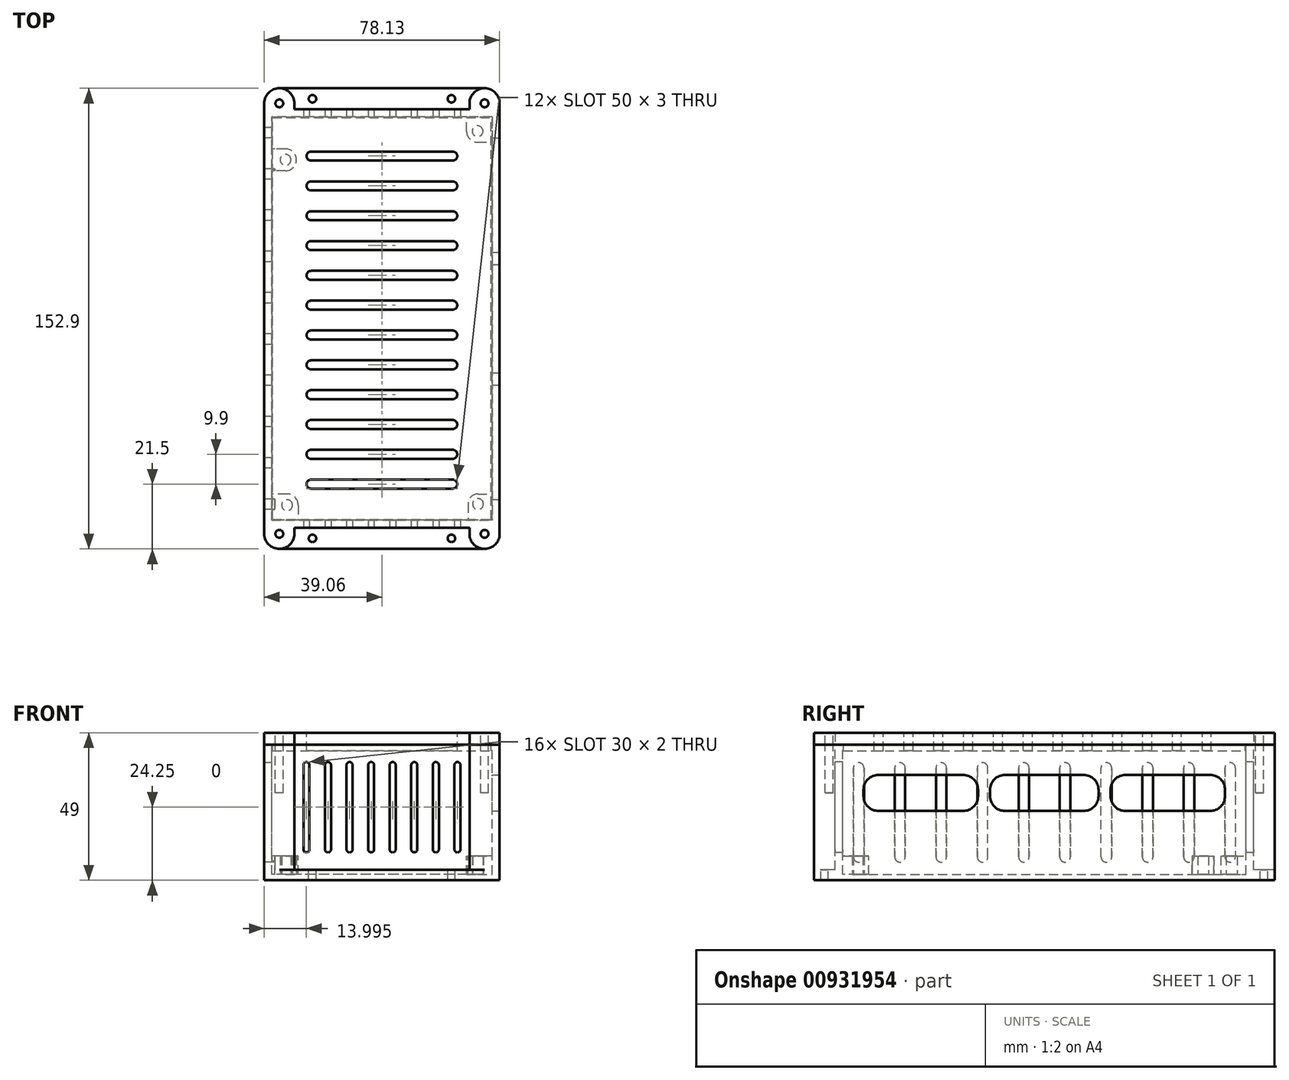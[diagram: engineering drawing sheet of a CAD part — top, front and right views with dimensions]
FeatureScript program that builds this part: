
annotation { "Feature Type Name" : "Feature", "Feature Type Description" : "" }
export const myFeature = defineFeature(function(context is Context, id is Id, definition is map)
    precondition{}
    {
        {
            var Q0;
            Q0=qCreatedBy(makeId("Top.planeOp"),FACE);
            var sketch = newSketch(context, id + "F0", { "sketchPlane" : qUnion([Q0])});
            skPoint(sketch, "E0.middle", {"position": v(0, 0) * mm});
            skLineSegment(sketch, "E1.0", {"start": v(33.87, 64.25) * mm, "end": v(-37.26, 64.25) * mm});
            skLineSegment(sketch, "E1.1", {"start": v(33.87, 64.25) * mm, "end": v(33.87, -67.65) * mm});
            skLineSegment(sketch, "E1.2", {"start": v(33.87, -67.65) * mm, "end": v(-37.26, -67.65) * mm});
            skLineSegment(sketch, "E1.3", {"start": v(-37.26, 64.25) * mm, "end": v(-37.26, -67.65) * mm});
            skLineSegment(sketch, "E2.0", {"start": v(37.37, -71.15) * mm, "end": v(-40.76, -71.15) * mm});
            skLineSegment(sketch, "E2.1", {"start": v(37.37, 67.75) * mm, "end": v(37.37, -71.15) * mm});
            skLineSegment(sketch, "E2.2", {"start": v(37.37, 67.75) * mm, "end": v(-40.76, 67.75) * mm});
            skLineSegment(sketch, "E2.3", {"start": v(-40.76, 67.75) * mm, "end": v(-40.76, -71.15) * mm});
            skSolve(sketch);
        }
        {
            var Q0;
            Q0 = qSketchRegion(id + "F0", true);
            extrude(context, id + "F1", {"entities" : qUnion([Q0]), "depth" : 25 * mm, "offsetDistance" : 25 * mm});
        }
        {
            var Q0;
            Q0=makeQuery(id+"F1.opExtrude","CAP_FACE",FACE,{"disambiguationData":[OSD([sQuery(id+"F0.wireOp",EDGE,"E1.0"),sQuery(id+"F0.wireOp",EDGE,"E1.1"),sQuery(id+"F0.wireOp",EDGE,"E1.2"),sQuery(id+"F0.wireOp",EDGE,"E1.3"),sQuery(id+"F0.wireOp",EDGE,"E2.0"),sQuery(id+"F0.wireOp",EDGE,"E2.1"),sQuery(id+"F0.wireOp",EDGE,"E2.2"),sQuery(id+"F0.wireOp",EDGE,"E2.3")])],"isStart":true});
            var sketch = newSketch(context, id + "F2", { "sketchPlane" : qUnion([Q0])});
            skLineSegment(sketch, "E3.bottom", {"start": v(-37.26, 67.65) * mm, "end": v(33.87, 67.65) * mm});
            skLineSegment(sketch, "E3.top", {"start": v(-37.26, -64.25) * mm, "end": v(33.87, -64.25) * mm});
            skLineSegment(sketch, "E3.left", {"start": v(-37.26, 67.65) * mm, "end": v(-37.26, -64.25) * mm});
            skLineSegment(sketch, "E3.right", {"start": v(33.87, 67.65) * mm, "end": v(33.87, -64.25) * mm});
            skSolve(sketch);
        }
        {
            var Q0;
            Q0 = qSketchRegion(id + "F2", true);
            extrude(context, id + "F3", {"entities" : qUnion([Q0]), "operationType" : NewBodyOperationType.ADD, "oppositeDirection" : true, "depth" : 2 * mm, "offsetDistance" : 25 * mm});
        }
        {
            var Q0;
            Q0=makeQuery(id+"F3.opExtrude","CAP_FACE",FACE,{"disambiguationData":[OSD([sQuery(id+"F2.wireOp",EDGE,"E3.bottom"),sQuery(id+"F2.wireOp",EDGE,"E3.top"),sQuery(id+"F2.wireOp",EDGE,"E3.left"),sQuery(id+"F2.wireOp",EDGE,"E3.right")])],"isStart":false});
            var sketch = newSketch(context, id + "F4", { "sketchPlane" : qUnion([Q0])});
            skPoint(sketch, "E4.middle", {"position": v(-1.7, -1.7) * mm});
            skCircle(sketch, "E5", {"center": v(-33.19, -63.64) * mm, "radius": 1.8 * mm});
            skCircle(sketch, "E6", {"center": v(30.17, -63.24) * mm, "radius": 1.8 * mm});
            skCircle(sketch, "E7", {"center": v(-33.69, 51) * mm, "radius": 1.8 * mm});
            skCircle(sketch, "E8", {"center": v(30.04, 60.5) * mm, "radius": 1.8 * mm});
            skLineSegment(sketch, "E9", {"start": v(26.86, -63.24) * mm, "end": v(26.86, -67.15) * mm});
            skArc(sketch, "E10", {"start": v(30.17, -59.93) * mm, "mid": v(27.83, -60.9) * mm, "end": v(26.86, -63.24) * mm});
            skLineSegment(sketch, "E11", {"start": v(30.17, -59.93) * mm, "end": v(33.3, -59.93) * mm});
            skLineSegment(sketch, "E12", {"start": v(33.3, -59.93) * mm, "end": v(33.87, -59.93) * mm});
            skLineSegment(sketch, "E13", {"start": v(26.86, -67.15) * mm, "end": v(26.86, -67.65) * mm});
            skLineSegment(sketch, "E14", {"start": v(-33.19, -59.93) * mm, "end": v(-36.7, -59.93) * mm});
            skLineSegment(sketch, "E15", {"start": v(-29.48, -63.64) * mm, "end": v(-29.48, -67.15) * mm});
            skArc(sketch, "E16.trimOffspring", {"start": v(-29.48, -63.64) * mm, "mid": v(-30.57, -61.02) * mm, "end": v(-33.19, -59.93) * mm});
            skPoint(sketch, "E17.orphan", {"position": v(-36.7, -67.15) * mm});
            skLineSegment(sketch, "E18", {"start": v(-36.7, -59.93) * mm, "end": v(-37.26, -59.93) * mm});
            skLineSegment(sketch, "E19", {"start": v(-29.48, -67.15) * mm, "end": v(-29.48, -67.65) * mm});
            skArc(sketch, "E20", {"start": v(-33.69, 47.38) * mm, "mid": v(-30.06, 51) * mm, "end": v(-33.69, 54.63) * mm});
            skLineSegment(sketch, "E21", {"start": v(-33.69, 54.63) * mm, "end": v(-36.7, 54.63) * mm});
            skLineSegment(sketch, "E22", {"start": v(-33.69, 47.38) * mm, "end": v(-36.7, 47.38) * mm});
            skArc(sketch, "E23", {"start": v(26.42, 60.5) * mm, "mid": v(27.48, 57.93) * mm, "end": v(30.04, 56.87) * mm});
            skLineSegment(sketch, "E24", {"start": v(26.42, 60.5) * mm, "end": v(26.42, 63.75) * mm});
            skLineSegment(sketch, "E25", {"start": v(30.04, 60.5) * mm, "end": v(30.04, 58.7) * mm});
            skLineSegment(sketch, "E26", {"start": v(30.04, 56.87) * mm, "end": v(33.87, 56.87) * mm});
            skLineSegment(sketch, "E27", {"start": v(26.42, 63.75) * mm, "end": v(26.42, 64.25) * mm});
            skLineSegment(sketch, "E28", {"start": v(-36.7, 54.63) * mm, "end": v(-37.26, 54.63) * mm});
            skLineSegment(sketch, "E29", {"start": v(-36.7, 47.38) * mm, "end": v(-37.26, 47.38) * mm});
            skLineSegment(sketch, "E30", {"start": v(-37.26, 47.38) * mm, "end": v(-37.26, 54.63) * mm});
            skLineSegment(sketch, "E31", {"start": v(33.87, 56.87) * mm, "end": v(33.87, 64.25) * mm});
            skLineSegment(sketch, "E32", {"start": v(33.87, 64.25) * mm, "end": v(26.42, 64.25) * mm});
            skLineSegment(sketch, "E33", {"start": v(33.87, -59.93) * mm, "end": v(33.87, -67.65) * mm});
            skLineSegment(sketch, "E34", {"start": v(33.87, -67.65) * mm, "end": v(26.86, -67.65) * mm});
            skLineSegment(sketch, "E35", {"start": v(-29.48, -67.65) * mm, "end": v(-37.26, -67.65) * mm});
            skLineSegment(sketch, "E36", {"start": v(-37.26, -67.65) * mm, "end": v(-37.26, -59.93) * mm});
            skSolve(sketch);
        }
        {
            var Q0;
            Q0 = qSketchRegion(id + "F4", true);
            extrude(context, id + "F5", {"entities" : qUnion([Q0]), "operationType" : NewBodyOperationType.ADD, "depth" : 6 * mm, "offsetDistance" : 25 * mm});
        }
        {
            var Q0;
            Q0=makeQuery(id+"F1.opExtrude","CAP_FACE",FACE,{"disambiguationData":[OSD([sQuery(id+"F0.wireOp",EDGE,"E1.0"),sQuery(id+"F0.wireOp",EDGE,"E1.1"),sQuery(id+"F0.wireOp",EDGE,"E1.2"),sQuery(id+"F0.wireOp",EDGE,"E1.3"),sQuery(id+"F0.wireOp",EDGE,"E2.0"),sQuery(id+"F0.wireOp",EDGE,"E2.1"),sQuery(id+"F0.wireOp",EDGE,"E2.2"),sQuery(id+"F0.wireOp",EDGE,"E2.3")])],"isStart":false});
            extrude(context, id + "F6", {"entities" : qUnion([Q0]), "operationType" : NewBodyOperationType.ADD, "depth" : 15 * mm, "offsetDistance" : 25 * mm});
        }
        {
            var Q0;
            Q0=makeQuery(id+"F6.opExtrude","CAP_FACE",FACE,{"disambiguationData":[OSD([sQuery(id+"F0.wireOp",EDGE,"E1.0"),sQuery(id+"F0.wireOp",EDGE,"E1.1"),sQuery(id+"F0.wireOp",EDGE,"E1.2"),sQuery(id+"F0.wireOp",EDGE,"E1.3"),sQuery(id+"F0.wireOp",EDGE,"E2.0"),sQuery(id+"F0.wireOp",EDGE,"E2.1"),sQuery(id+"F0.wireOp",EDGE,"E2.2"),sQuery(id+"F0.wireOp",EDGE,"E2.3")])],"isStart":false});
            extrude(context, id + "F7", {"entities" : qUnion([Q0]), "operationType" : NewBodyOperationType.ADD, "depth" : 5 * mm, "offsetDistance" : 25 * mm});
        }
        {
            var Q0;
            {var subQ0=sQuery(id+"F0.wireOp",EDGE,"E2.1");Q0=makeQuery(id+"F7.boolean.opBoolean","MERGE",FACE,{"derivedFrom":[makeQuery(id+"F6.boolean.opBoolean","MERGE",FACE,{"derivedFrom":[makeQuery(id+"F1.opExtrude","SWEPT_FACE",FACE,{"disambiguationData":[OSD([subQ0])]}),makeQuery(id+"F6.opExtrude","SWEPT_FACE",FACE,{"disambiguationData":[OSD([subQ0])]})]}),makeQuery(id+"F7.opExtrude","SWEPT_FACE",FACE,{"disambiguationData":[OSD([subQ0])]})]});}
            var sketch = newSketch(context, id + "F8", { "sketchPlane" : qUnion([Q0])});
            skLineSegment(sketch, "E37", {"start": v(-1.7, 35) * mm, "end": v(11.3, 35) * mm});
            skLineSegment(sketch, "E38", {"start": v(58.3, 30) * mm, "end": v(58.3, 28) * mm});
            skLineSegment(sketch, "E39", {"start": v(53.3, 23) * mm, "end": v(25.3, 23) * mm});
            skLineSegment(sketch, "E40", {"start": v(-61.7, 28) * mm, "end": v(-61.7, 30) * mm});
            skLineSegment(sketch, "E41", {"start": v(-56.7, 35) * mm, "end": v(-28.7, 35) * mm});
            skPoint(sketch, "E42.endSnap0", {"position": v(-31.7, 35) * mm});
            skLineSegment(sketch, "E43", {"start": v(-56.7, 23) * mm, "end": v(-28.7, 23) * mm});
            skLineSegment(sketch, "E44", {"start": v(-14.7, 35) * mm, "end": v(11.3, 35) * mm});
            skLineSegment(sketch, "E45.0", {"start": v(16.3, 30) * mm, "end": v(16.3, 28) * mm});
            skLineSegment(sketch, "E46.0", {"start": v(20.3, 30) * mm, "end": v(20.3, 28) * mm});
            skLineSegment(sketch, "E47.0", {"start": v(-19.7, 28) * mm, "end": v(-19.7, 30) * mm});
            skLineSegment(sketch, "E48.0", {"start": v(-23.7, 28) * mm, "end": v(-23.7, 30) * mm});
            skLineSegment(sketch, "E49.trimOffspring", {"start": v(-14.7, 35) * mm, "end": v(-1.7, 35) * mm});
            skLineSegment(sketch, "E50.trimOffspring", {"start": v(-28.7, 23) * mm, "end": v(-56.7, 23) * mm});
            skLineSegment(sketch, "E51.trimOffspring", {"start": v(25.3, 35) * mm, "end": v(53.3, 35) * mm});
            skLineSegment(sketch, "E52.trimOffspring", {"start": v(11.3, 23) * mm, "end": v(-14.7, 23) * mm});
            skPoint(sketch, "E53.visualSharp", {"position": v(-19.7, 35) * mm});
            skArc(sketch, "E53.filletArc", {"start": v(-14.7, 35) * mm, "mid": v(-18.24, 33.54) * mm, "end": v(-19.7, 30) * mm});
            skPoint(sketch, "E54.visualSharp", {"position": v(-19.7, 23) * mm});
            skArc(sketch, "E54.filletArc", {"start": v(-19.7, 28) * mm, "mid": v(-18.24, 24.46) * mm, "end": v(-14.7, 23) * mm});
            skPoint(sketch, "E55.visualSharp", {"position": v(16.3, 35) * mm});
            skArc(sketch, "E55.filletArc", {"start": v(16.3, 30) * mm, "mid": v(14.84, 33.54) * mm, "end": v(11.3, 35) * mm});
            skPoint(sketch, "E56.visualSharp", {"position": v(16.3, 23) * mm});
            skArc(sketch, "E56.filletArc", {"start": v(11.3, 23) * mm, "mid": v(14.84, 24.46) * mm, "end": v(16.3, 28) * mm});
            skPoint(sketch, "E57.visualSharp", {"position": v(20.3, 23) * mm});
            skArc(sketch, "E57.filletArc", {"start": v(20.3, 28) * mm, "mid": v(21.76, 24.46) * mm, "end": v(25.3, 23) * mm});
            skPoint(sketch, "E58.visualSharp", {"position": v(20.3, 35) * mm});
            skArc(sketch, "E58.filletArc", {"start": v(25.3, 35) * mm, "mid": v(21.76, 33.54) * mm, "end": v(20.3, 30) * mm});
            skPoint(sketch, "E59.visualSharp", {"position": v(58.3, 35) * mm});
            skArc(sketch, "E59.filletArc", {"start": v(58.3, 30) * mm, "mid": v(56.84, 33.54) * mm, "end": v(53.3, 35) * mm});
            skPoint(sketch, "E60.visualSharp", {"position": v(58.3, 23) * mm});
            skArc(sketch, "E60.filletArc", {"start": v(53.3, 23) * mm, "mid": v(56.84, 24.46) * mm, "end": v(58.3, 28) * mm});
            skPoint(sketch, "E61.visualSharp", {"position": v(-23.7, 35) * mm});
            skArc(sketch, "E61.filletArc", {"start": v(-23.7, 30) * mm, "mid": v(-25.16, 33.54) * mm, "end": v(-28.7, 35) * mm});
            skPoint(sketch, "E62.visualSharp", {"position": v(-23.7, 23) * mm});
            skArc(sketch, "E62.filletArc", {"start": v(-28.7, 23) * mm, "mid": v(-25.16, 24.46) * mm, "end": v(-23.7, 28) * mm});
            skPoint(sketch, "E63.visualSharp", {"position": v(-61.7, 35) * mm});
            skArc(sketch, "E63.filletArc", {"start": v(-56.7, 35) * mm, "mid": v(-60.24, 33.54) * mm, "end": v(-61.7, 30) * mm});
            skPoint(sketch, "E64.visualSharp", {"position": v(-61.7, 23) * mm});
            skArc(sketch, "E64.filletArc", {"start": v(-61.7, 28) * mm, "mid": v(-60.24, 24.46) * mm, "end": v(-56.7, 23) * mm});
            skSolve(sketch);
        }
        {
            var Q0;
            Q0 = qSketchRegion(id + "F8", true);
            extrude(context, id + "F9", {"entities" : qUnion([Q0]), "operationType" : NewBodyOperationType.REMOVE, "oppositeDirection" : true, "depth" : 25 * mm, "offsetDistance" : 25 * mm});
        }
        {
            var Q0;
            {var subQ0=sQuery(id+"F0.wireOp",EDGE,"E2.3");Q0=makeQuery(id+"F7.boolean.opBoolean","MERGE",FACE,{"derivedFrom":[makeQuery(id+"F6.boolean.opBoolean","MERGE",FACE,{"derivedFrom":[makeQuery(id+"F1.opExtrude","SWEPT_FACE",FACE,{"disambiguationData":[OSD([subQ0])]}),makeQuery(id+"F6.opExtrude","SWEPT_FACE",FACE,{"disambiguationData":[OSD([subQ0])]})]}),makeQuery(id+"F7.opExtrude","SWEPT_FACE",FACE,{"disambiguationData":[OSD([subQ0])]})]});}
            var sketch = newSketch(context, id + "F10", { "sketchPlane" : qUnion([Q0])});
            skLineSegment(sketch, "E65.0", {"start": v(-60.34, 39) * mm, "end": v(-59.66, 39) * mm});
            skLineSegment(sketch, "E66.right", {"start": v(-58.25, 37.28) * mm, "end": v(-58.25, 7.75) * mm});
            skArc(sketch, "E67", {"start": v(-58.25, 37.28) * mm, "mid": v(-60, 39.03) * mm, "end": v(-61.75, 37.28) * mm});
            skPoint(sketch, "E68.center.orphan", {"position": v(-60, 39) * mm});
            skArc(sketch, "E69", {"start": v(-61.75, 7.75) * mm, "mid": v(-60, 6) * mm, "end": v(-58.25, 7.75) * mm});
            skPoint(sketch, "E70.center.orphan", {"position": v(-60, 6) * mm});
            skPoint(sketch, "E71.1.0.0", {"position": v(-46.3, 39) * mm});
            skPoint(sketch, "E71.1.0.1", {"position": v(-46.3, 6) * mm});
            skLineSegment(sketch, "E71.1.0.2", {"start": v(-48.05, 37.28) * mm, "end": v(-48.05, 7.75) * mm});
            skLineSegment(sketch, "E71.1.0.4", {"start": v(-44.55, 37.28) * mm, "end": v(-44.55, 7.75) * mm});
            skArc(sketch, "E71.1.0.5", {"start": v(-48.05, 7.75) * mm, "mid": v(-46.3, 6) * mm, "end": v(-44.55, 7.75) * mm});
            skLineSegment(sketch, "E71.1.0.6", {"start": v(-48.05, 37.28) * mm, "end": v(-48.05, 7.75) * mm});
            skArc(sketch, "E71.1.0.7", {"start": v(-44.55, 37.28) * mm, "mid": v(-46.3, 39.03) * mm, "end": v(-48.05, 37.28) * mm});
            skLineSegment(sketch, "E71.1.0.8", {"start": v(-46.64, 39) * mm, "end": v(-45.96, 39) * mm});
            skLineSegment(sketch, "E71.1.0.9", {"start": v(-46.64, 39) * mm, "end": v(-45.96, 39) * mm});
            skPoint(sketch, "E71.2.0.0", {"position": v(-32.6, 39) * mm});
            skPoint(sketch, "E71.2.0.1", {"position": v(-32.6, 6) * mm});
            skLineSegment(sketch, "E71.2.0.2", {"start": v(-34.35, 37.28) * mm, "end": v(-34.35, 7.75) * mm});
            skLineSegment(sketch, "E71.2.0.4", {"start": v(-30.85, 37.28) * mm, "end": v(-30.85, 7.75) * mm});
            skArc(sketch, "E71.2.0.5", {"start": v(-34.35, 7.75) * mm, "mid": v(-32.6, 6) * mm, "end": v(-30.85, 7.75) * mm});
            skLineSegment(sketch, "E71.2.0.6", {"start": v(-34.35, 37.28) * mm, "end": v(-34.35, 7.75) * mm});
            skArc(sketch, "E71.2.0.7", {"start": v(-30.85, 37.28) * mm, "mid": v(-32.6, 39.03) * mm, "end": v(-34.35, 37.28) * mm});
            skLineSegment(sketch, "E71.2.0.8", {"start": v(-32.94, 39) * mm, "end": v(-32.26, 39) * mm});
            skLineSegment(sketch, "E71.2.0.9", {"start": v(-32.94, 39) * mm, "end": v(-32.26, 39) * mm});
            skPoint(sketch, "E71.3.0.0", {"position": v(-18.9, 39) * mm});
            skPoint(sketch, "E71.3.0.1", {"position": v(-18.9, 6) * mm});
            skLineSegment(sketch, "E71.3.0.2", {"start": v(-20.65, 37.28) * mm, "end": v(-20.65, 7.75) * mm});
            skLineSegment(sketch, "E71.3.0.4", {"start": v(-17.15, 37.28) * mm, "end": v(-17.15, 7.75) * mm});
            skArc(sketch, "E71.3.0.5", {"start": v(-20.65, 7.75) * mm, "mid": v(-18.9, 6) * mm, "end": v(-17.15, 7.75) * mm});
            skLineSegment(sketch, "E71.3.0.6", {"start": v(-20.65, 37.28) * mm, "end": v(-20.65, 7.75) * mm});
            skArc(sketch, "E71.3.0.7", {"start": v(-17.15, 37.28) * mm, "mid": v(-18.9, 39.03) * mm, "end": v(-20.65, 37.28) * mm});
            skLineSegment(sketch, "E71.3.0.8", {"start": v(-19.24, 39) * mm, "end": v(-18.56, 39) * mm});
            skLineSegment(sketch, "E71.3.0.9", {"start": v(-19.24, 39) * mm, "end": v(-18.56, 39) * mm});
            skPoint(sketch, "E71.4.0.0", {"position": v(-5.2, 39) * mm});
            skPoint(sketch, "E71.4.0.1", {"position": v(-5.2, 6) * mm});
            skLineSegment(sketch, "E71.4.0.2", {"start": v(-6.95, 37.28) * mm, "end": v(-6.95, 7.75) * mm});
            skLineSegment(sketch, "E71.4.0.4", {"start": v(-3.45, 37.28) * mm, "end": v(-3.45, 7.75) * mm});
            skArc(sketch, "E71.4.0.5", {"start": v(-6.95, 7.75) * mm, "mid": v(-5.2, 6) * mm, "end": v(-3.45, 7.75) * mm});
            skLineSegment(sketch, "E71.4.0.6", {"start": v(-6.95, 37.28) * mm, "end": v(-6.95, 7.75) * mm});
            skArc(sketch, "E71.4.0.7", {"start": v(-3.45, 37.28) * mm, "mid": v(-5.2, 39.03) * mm, "end": v(-6.95, 37.28) * mm});
            skLineSegment(sketch, "E71.4.0.8", {"start": v(-5.54, 39) * mm, "end": v(-4.86, 39) * mm});
            skLineSegment(sketch, "E71.4.0.9", {"start": v(-5.54, 39) * mm, "end": v(-4.86, 39) * mm});
            skPoint(sketch, "E71.5.0.0", {"position": v(8.5, 39) * mm});
            skPoint(sketch, "E71.5.0.1", {"position": v(8.5, 6) * mm});
            skLineSegment(sketch, "E71.5.0.2", {"start": v(6.75, 37.28) * mm, "end": v(6.75, 7.75) * mm});
            skLineSegment(sketch, "E71.5.0.4", {"start": v(10.25, 37.28) * mm, "end": v(10.25, 7.75) * mm});
            skArc(sketch, "E71.5.0.5", {"start": v(6.75, 7.75) * mm, "mid": v(8.5, 6) * mm, "end": v(10.25, 7.75) * mm});
            skLineSegment(sketch, "E71.5.0.6", {"start": v(6.75, 37.28) * mm, "end": v(6.75, 7.75) * mm});
            skArc(sketch, "E71.5.0.7", {"start": v(10.25, 37.28) * mm, "mid": v(8.5, 39.03) * mm, "end": v(6.75, 37.28) * mm});
            skLineSegment(sketch, "E71.5.0.8", {"start": v(8.16, 39) * mm, "end": v(8.84, 39) * mm});
            skLineSegment(sketch, "E71.5.0.9", {"start": v(8.16, 39) * mm, "end": v(8.84, 39) * mm});
            skPoint(sketch, "E71.6.0.0", {"position": v(22.2, 39) * mm});
            skPoint(sketch, "E71.6.0.1", {"position": v(22.2, 6) * mm});
            skLineSegment(sketch, "E71.6.0.2", {"start": v(20.45, 37.28) * mm, "end": v(20.45, 7.75) * mm});
            skLineSegment(sketch, "E71.6.0.4", {"start": v(23.95, 37.28) * mm, "end": v(23.95, 7.75) * mm});
            skArc(sketch, "E71.6.0.5", {"start": v(20.45, 7.75) * mm, "mid": v(22.2, 6) * mm, "end": v(23.95, 7.75) * mm});
            skLineSegment(sketch, "E71.6.0.6", {"start": v(20.45, 37.28) * mm, "end": v(20.45, 7.75) * mm});
            skArc(sketch, "E71.6.0.7", {"start": v(23.95, 37.28) * mm, "mid": v(22.2, 39.03) * mm, "end": v(20.45, 37.28) * mm});
            skLineSegment(sketch, "E71.6.0.8", {"start": v(21.86, 39) * mm, "end": v(22.54, 39) * mm});
            skLineSegment(sketch, "E71.6.0.9", {"start": v(21.86, 39) * mm, "end": v(22.54, 39) * mm});
            skPoint(sketch, "E71.7.0.0", {"position": v(35.9, 39) * mm});
            skPoint(sketch, "E71.7.0.1", {"position": v(35.9, 6) * mm});
            skLineSegment(sketch, "E71.7.0.2", {"start": v(34.15, 37.28) * mm, "end": v(34.15, 7.75) * mm});
            skLineSegment(sketch, "E71.7.0.4", {"start": v(37.65, 37.28) * mm, "end": v(37.65, 7.75) * mm});
            skArc(sketch, "E71.7.0.5", {"start": v(34.15, 7.75) * mm, "mid": v(35.9, 6) * mm, "end": v(37.65, 7.75) * mm});
            skLineSegment(sketch, "E71.7.0.6", {"start": v(34.15, 37.28) * mm, "end": v(34.15, 7.75) * mm});
            skArc(sketch, "E71.7.0.7", {"start": v(37.65, 37.28) * mm, "mid": v(35.9, 39.03) * mm, "end": v(34.15, 37.28) * mm});
            skLineSegment(sketch, "E71.7.0.8", {"start": v(35.56, 39) * mm, "end": v(36.24, 39) * mm});
            skLineSegment(sketch, "E71.7.0.9", {"start": v(35.56, 39) * mm, "end": v(36.24, 39) * mm});
            skPoint(sketch, "E71.8.0.0", {"position": v(49.6, 39) * mm});
            skPoint(sketch, "E71.8.0.1", {"position": v(49.6, 6) * mm});
            skLineSegment(sketch, "E71.8.0.2", {"start": v(47.85, 37.28) * mm, "end": v(47.85, 7.75) * mm});
            skLineSegment(sketch, "E71.8.0.4", {"start": v(51.35, 37.28) * mm, "end": v(51.35, 7.75) * mm});
            skArc(sketch, "E71.8.0.5", {"start": v(47.85, 7.75) * mm, "mid": v(49.6, 6) * mm, "end": v(51.35, 7.75) * mm});
            skLineSegment(sketch, "E71.8.0.6", {"start": v(47.85, 37.28) * mm, "end": v(47.85, 7.75) * mm});
            skArc(sketch, "E71.8.0.7", {"start": v(51.35, 37.28) * mm, "mid": v(49.6, 39.03) * mm, "end": v(47.85, 37.28) * mm});
            skLineSegment(sketch, "E71.8.0.8", {"start": v(49.26, 39) * mm, "end": v(49.94, 39) * mm});
            skLineSegment(sketch, "E71.8.0.9", {"start": v(49.26, 39) * mm, "end": v(49.94, 39) * mm});
            skPoint(sketch, "E71.9.0.0", {"position": v(63.3, 39) * mm});
            skPoint(sketch, "E71.9.0.1", {"position": v(63.3, 6) * mm});
            skLineSegment(sketch, "E71.9.0.2", {"start": v(61.55, 37.28) * mm, "end": v(61.55, 7.75) * mm});
            skLineSegment(sketch, "E71.9.0.4", {"start": v(65.05, 37.28) * mm, "end": v(65.05, 7.75) * mm});
            skArc(sketch, "E71.9.0.5", {"start": v(61.55, 7.75) * mm, "mid": v(63.3, 6) * mm, "end": v(65.05, 7.75) * mm});
            skLineSegment(sketch, "E71.9.0.6", {"start": v(61.55, 37.28) * mm, "end": v(61.55, 7.75) * mm});
            skArc(sketch, "E71.9.0.7", {"start": v(65.05, 37.28) * mm, "mid": v(63.3, 39.03) * mm, "end": v(61.55, 37.28) * mm});
            skLineSegment(sketch, "E71.9.0.8", {"start": v(62.96, 39) * mm, "end": v(63.64, 39) * mm});
            skLineSegment(sketch, "E71.9.0.9", {"start": v(62.96, 39) * mm, "end": v(63.64, 39) * mm});
            skLineSegment(sketch, "E72", {"start": v(-61.75, 7.75) * mm, "end": v(-61.75, 37.28) * mm});
            skSolve(sketch);
        }
        {
            var Q0;
            Q0 = qSketchRegion(id + "F10", true);
            var Q1;
            {var subQ0=sQuery(id+"F0.wireOp",EDGE,"E1.3");Q1=makeQuery(id+"F7.boolean.opBoolean","MERGE",FACE,{"derivedFrom":[makeQuery(id+"F6.boolean.opBoolean","MERGE",FACE,{"derivedFrom":[makeQuery(id+"F1.opExtrude","SWEPT_FACE",FACE,{"disambiguationData":[OSD([subQ0])]}),makeQuery(id+"F6.opExtrude","SWEPT_FACE",FACE,{"disambiguationData":[OSD([subQ0])]})]}),makeQuery(id+"F7.opExtrude","SWEPT_FACE",FACE,{"disambiguationData":[OSD([subQ0])]})]});}
            extrude(context, id + "F11", {"entities" : qUnion([Q0]), "operationType" : NewBodyOperationType.REMOVE, "endBound" : BoundingType.UP_TO_SURFACE, "oppositeDirection" : true, "depth" : 25 * mm, "endBoundEntityFace" : qUnion([Q1]), "offsetDistance" : 25 * mm});
        }
        {
            var Q0;
            Q0=makeQuery(id+"F7.opExtrude","CAP_FACE",FACE,{"disambiguationData":[OSD([sQuery(id+"F0.wireOp",EDGE,"E1.0"),sQuery(id+"F0.wireOp",EDGE,"E1.1"),sQuery(id+"F0.wireOp",EDGE,"E1.2"),sQuery(id+"F0.wireOp",EDGE,"E1.3"),sQuery(id+"F0.wireOp",EDGE,"E2.0"),sQuery(id+"F0.wireOp",EDGE,"E2.1"),sQuery(id+"F0.wireOp",EDGE,"E2.2"),sQuery(id+"F0.wireOp",EDGE,"E2.3")])],"isStart":false});
            var sketch = newSketch(context, id + "F12", { "sketchPlane" : qUnion([Q0])});
            skLineSegment(sketch, "E73.bottom", {"start": v(-37.26, 64.25) * mm, "end": v(33.87, 64.25) * mm});
            skLineSegment(sketch, "E73.top", {"start": v(-37.26, -67.65) * mm, "end": v(33.87, -67.65) * mm});
            skLineSegment(sketch, "E73.left", {"start": v(-37.26, 64.25) * mm, "end": v(-37.26, -67.65) * mm});
            skLineSegment(sketch, "E73.right", {"start": v(33.87, 64.25) * mm, "end": v(33.87, -67.65) * mm});
            skLineSegment(sketch, "E74.0", {"start": v(34.87, 65.25) * mm, "end": v(34.87, -68.65) * mm});
            skLineSegment(sketch, "E74.1", {"start": v(-38.26, 65.25) * mm, "end": v(34.87, 65.25) * mm});
            skLineSegment(sketch, "E74.2", {"start": v(-38.26, 65.25) * mm, "end": v(-38.26, -68.65) * mm});
            skLineSegment(sketch, "E74.3", {"start": v(-38.26, -68.65) * mm, "end": v(34.87, -68.65) * mm});
            skSolve(sketch);
        }
        {
            var Q0;
            Q0 = qSketchRegion(id + "F12", true);
            var Q1;
            Q1=makeQuery(id+"F5.opExtrude","CAP_FACE",FACE,{"disambiguationData":[OSD([sQuery(id+"F4.wireOp",EDGE,"E7"),sQuery(id+"F4.wireOp",EDGE,"E20"),sQuery(id+"F4.wireOp",EDGE,"E21"),sQuery(id+"F4.wireOp",EDGE,"E22"),sQuery(id+"F4.wireOp",EDGE,"E28"),sQuery(id+"F4.wireOp",EDGE,"E29"),sQuery(id+"F4.wireOp",EDGE,"E30")])],"isStart":false});
            extrude(context, id + "F13", {"entities" : qUnion([Q0]), "operationType" : NewBodyOperationType.REMOVE, "endBound" : BoundingType.UP_TO_SURFACE, "oppositeDirection" : true, "depth" : 25 * mm, "endBoundEntityFace" : qUnion([Q1]), "offsetDistance" : 25 * mm});
        }
        {
            var Q0;
            Q0=makeQuery(id+"F13.boolean.opBoolean","MERGE",FACE,{"derivedFrom":[makeQuery(id+"F5.opExtrude","CAP_FACE",FACE,{"disambiguationData":[OSD([sQuery(id+"F4.wireOp",EDGE,"E5"),sQuery(id+"F4.wireOp",EDGE,"E14"),sQuery(id+"F4.wireOp",EDGE,"E15"),sQuery(id+"F4.wireOp",EDGE,"E16.trimOffspring"),sQuery(id+"F4.wireOp",EDGE,"E18"),sQuery(id+"F4.wireOp",EDGE,"E19"),sQuery(id+"F4.wireOp",EDGE,"E35"),sQuery(id+"F4.wireOp",EDGE,"E36")])],"isStart":false}),makeQuery(id+"F5.opExtrude","CAP_FACE",FACE,{"disambiguationData":[OSD([sQuery(id+"F4.wireOp",EDGE,"E6"),sQuery(id+"F4.wireOp",EDGE,"E9"),sQuery(id+"F4.wireOp",EDGE,"E10"),sQuery(id+"F4.wireOp",EDGE,"E11"),sQuery(id+"F4.wireOp",EDGE,"E12"),sQuery(id+"F4.wireOp",EDGE,"E13"),sQuery(id+"F4.wireOp",EDGE,"E33"),sQuery(id+"F4.wireOp",EDGE,"E34")])],"isStart":false}),makeQuery(id+"F5.opExtrude","CAP_FACE",FACE,{"disambiguationData":[OSD([sQuery(id+"F4.wireOp",EDGE,"E8"),sQuery(id+"F4.wireOp",EDGE,"E23"),sQuery(id+"F4.wireOp",EDGE,"E24"),sQuery(id+"F4.wireOp",EDGE,"E26"),sQuery(id+"F4.wireOp",EDGE,"E27"),sQuery(id+"F4.wireOp",EDGE,"E31"),sQuery(id+"F4.wireOp",EDGE,"E32")])],"isStart":false})],"fromTools":[makeQuery(id+"F13.opExtrude","CAP_FACE",FACE,{"disambiguationData":[OSD([sQuery(id+"F12.wireOp",EDGE,"E73.bottom"),sQuery(id+"F12.wireOp",EDGE,"E73.top"),sQuery(id+"F12.wireOp",EDGE,"E73.left"),sQuery(id+"F12.wireOp",EDGE,"E73.right"),sQuery(id+"F12.wireOp",EDGE,"E74.0"),sQuery(id+"F12.wireOp",EDGE,"E74.1"),sQuery(id+"F12.wireOp",EDGE,"E74.2"),sQuery(id+"F12.wireOp",EDGE,"E74.3")])],"isStart":false})]});
            var sketch = newSketch(context, id + "F14", { "sketchPlane" : qUnion([Q0])});
            skLineSegment(sketch, "E75", {"start": v(-38.26, 65.25) * mm, "end": v(26.42, 65.25) * mm});
            skLineSegment(sketch, "E76", {"start": v(26.42, 65.25) * mm, "end": v(26.42, 64.25) * mm});
            skLineSegment(sketch, "E77", {"start": v(26.42, 64.25) * mm, "end": v(-37.26, 64.25) * mm});
            skLineSegment(sketch, "E78", {"start": v(-37.26, 64.25) * mm, "end": v(-37.26, 54.64) * mm});
            skLineSegment(sketch, "E79", {"start": v(-37.26, 54.64) * mm, "end": v(-38.26, 54.64) * mm});
            skLineSegment(sketch, "E80", {"start": v(-38.26, 54.64) * mm, "end": v(-38.26, 65.25) * mm});
            skLineSegment(sketch, "E81", {"start": v(-29.48, -67.65) * mm, "end": v(-29.48, -68.65) * mm});
            skLineSegment(sketch, "E82", {"start": v(-29.48, -68.65) * mm, "end": v(26.86, -68.65) * mm});
            skLineSegment(sketch, "E83", {"start": v(26.86, -68.65) * mm, "end": v(26.86, -67.65) * mm});
            skLineSegment(sketch, "E84", {"start": v(26.86, -67.65) * mm, "end": v(-29.48, -67.65) * mm});
            skLineSegment(sketch, "E85", {"start": v(33.87, -59.93) * mm, "end": v(34.87, -59.93) * mm});
            skLineSegment(sketch, "E86", {"start": v(34.87, -59.93) * mm, "end": v(34.87, 56.87) * mm});
            skLineSegment(sketch, "E87", {"start": v(34.87, 56.87) * mm, "end": v(33.87, 56.87) * mm});
            skLineSegment(sketch, "E88", {"start": v(33.87, 56.87) * mm, "end": v(33.87, -59.93) * mm});
            skLineSegment(sketch, "E89", {"start": v(-37.26, -59.93) * mm, "end": v(-38.26, -59.93) * mm});
            skLineSegment(sketch, "E90", {"start": v(-38.26, -59.93) * mm, "end": v(-38.26, 47.33) * mm});
            skLineSegment(sketch, "E91", {"start": v(-38.26, 47.33) * mm, "end": v(-37.26, 47.33) * mm});
            skLineSegment(sketch, "E92", {"start": v(-37.26, 47.33) * mm, "end": v(-37.26, -59.93) * mm});
            skSolve(sketch);
        }
        {
            var Q0;
            Q0 = qSketchRegion(id + "F14", true);
            var Q1;
            Q1=makeQuery(id+"F5.boolean.opBoolean","SPLIT",FACE,{"disambiguationData":[TD([makeQuery(id+"F1.opExtrude","SWEPT_FACE",FACE,{"disambiguationData":[OSD([sQuery(id+"F0.wireOp",EDGE,"E1.0")])]})])],"derivedFrom":makeQuery(id+"F3.opExtrude","CAP_FACE",FACE,{"disambiguationData":[OSD([sQuery(id+"F2.wireOp",EDGE,"E3.bottom"),sQuery(id+"F2.wireOp",EDGE,"E3.top"),sQuery(id+"F2.wireOp",EDGE,"E3.left"),sQuery(id+"F2.wireOp",EDGE,"E3.right")])],"isStart":false})});
            extrude(context, id + "F15", {"entities" : qUnion([Q0]), "operationType" : NewBodyOperationType.REMOVE, "endBound" : BoundingType.UP_TO_SURFACE, "oppositeDirection" : true, "depth" : 25 * mm, "endBoundEntityFace" : qUnion([Q1]), "offsetDistance" : 25 * mm});
        }
        {
            var Q0;
            Q0=makeQuery(id+"F7.opExtrude","CAP_FACE",FACE,{"disambiguationData":[OSD([sQuery(id+"F0.wireOp",EDGE,"E1.0"),sQuery(id+"F0.wireOp",EDGE,"E1.1"),sQuery(id+"F0.wireOp",EDGE,"E1.2"),sQuery(id+"F0.wireOp",EDGE,"E1.3"),sQuery(id+"F0.wireOp",EDGE,"E2.0"),sQuery(id+"F0.wireOp",EDGE,"E2.1"),sQuery(id+"F0.wireOp",EDGE,"E2.2"),sQuery(id+"F0.wireOp",EDGE,"E2.3")])],"isStart":false});
            var sketch = newSketch(context, id + "F16", { "sketchPlane" : qUnion([Q0])});
            skLineSegment(sketch, "E93", {"start": v(-40.76, 67.75) * mm, "end": v(-40.76, 69.75) * mm});
            skLineSegment(sketch, "E94", {"start": v(-30.76, 69.75) * mm, "end": v(-30.76, 67.75) * mm});
            skLineSegment(sketch, "E95.bottom", {"start": v(37.37, 67.75) * mm, "end": v(27.37, 67.75) * mm});
            skLineSegment(sketch, "E95.left", {"start": v(37.37, 67.75) * mm, "end": v(37.37, 69.75) * mm});
            skLineSegment(sketch, "E95.right", {"start": v(27.37, 67.75) * mm, "end": v(27.37, 69.75) * mm});
            skLineSegment(sketch, "E96.bottom", {"start": v(-40.76, -71.15) * mm, "end": v(-30.76, -71.15) * mm});
            skLineSegment(sketch, "E96.left", {"start": v(-40.76, -71.15) * mm, "end": v(-40.76, -73.15) * mm});
            skLineSegment(sketch, "E96.right", {"start": v(-30.76, -71.15) * mm, "end": v(-30.76, -73.15) * mm});
            skLineSegment(sketch, "E97.bottom", {"start": v(37.37, -71.15) * mm, "end": v(27.37, -71.15) * mm});
            skLineSegment(sketch, "E97.left", {"start": v(37.37, -71.15) * mm, "end": v(37.37, -73.15) * mm});
            skLineSegment(sketch, "E97.right", {"start": v(27.37, -71.15) * mm, "end": v(27.37, -73.15) * mm});
            skArc(sketch, "E98", {"start": v(-30.76, 69.75) * mm, "mid": v(-35.76, 74.75) * mm, "end": v(-40.76, 69.75) * mm});
            skArc(sketch, "E99", {"start": v(37.37, 69.75) * mm, "mid": v(32.37, 74.75) * mm, "end": v(27.37, 69.75) * mm});
            skArc(sketch, "E100", {"start": v(27.37, -73.15) * mm, "mid": v(32.37, -78.15) * mm, "end": v(37.37, -73.15) * mm});
            skArc(sketch, "E101", {"start": v(-40.76, -73.15) * mm, "mid": v(-35.76, -78.15) * mm, "end": v(-30.76, -73.15) * mm});
            skLineSegment(sketch, "E102", {"start": v(-30.76, 67.75) * mm, "end": v(-40.76, 67.75) * mm});
            skSolve(sketch);
        }
        {
            var Q0;
            Q0 = qSketchRegion(id + "F16", true);
            var Q1;
            Q1=makeQuery(id+"F3.boolean.opBoolean","MERGE",FACE,{"derivedFrom":[makeQuery(id+"F1.opExtrude","CAP_FACE",FACE,{"disambiguationData":[OSD([sQuery(id+"F0.wireOp",EDGE,"E1.0"),sQuery(id+"F0.wireOp",EDGE,"E1.1"),sQuery(id+"F0.wireOp",EDGE,"E1.2"),sQuery(id+"F0.wireOp",EDGE,"E1.3"),sQuery(id+"F0.wireOp",EDGE,"E2.0"),sQuery(id+"F0.wireOp",EDGE,"E2.1"),sQuery(id+"F0.wireOp",EDGE,"E2.2"),sQuery(id+"F0.wireOp",EDGE,"E2.3")])],"isStart":true}),makeQuery(id+"F3.opExtrude","CAP_FACE",FACE,{"disambiguationData":[OSD([sQuery(id+"F2.wireOp",EDGE,"E3.bottom"),sQuery(id+"F2.wireOp",EDGE,"E3.top"),sQuery(id+"F2.wireOp",EDGE,"E3.left"),sQuery(id+"F2.wireOp",EDGE,"E3.right")])],"isStart":true})]});
            extrude(context, id + "F17", {"entities" : qUnion([Q0]), "operationType" : NewBodyOperationType.ADD, "endBound" : BoundingType.UP_TO_SURFACE, "oppositeDirection" : true, "depth" : 25 * mm, "endBoundEntityFace" : qUnion([Q1]), "offsetDistance" : 25 * mm});
        }
        {
            var Q0;
            Q0=makeQuery(id+"F17.boolean.opBoolean","MERGE",FACE,{"derivedFrom":[makeQuery(id+"F7.opExtrude","CAP_FACE",FACE,{"disambiguationData":[OSD([sQuery(id+"F0.wireOp",EDGE,"E1.0"),sQuery(id+"F0.wireOp",EDGE,"E1.1"),sQuery(id+"F0.wireOp",EDGE,"E1.2"),sQuery(id+"F0.wireOp",EDGE,"E1.3"),sQuery(id+"F0.wireOp",EDGE,"E2.0"),sQuery(id+"F0.wireOp",EDGE,"E2.1"),sQuery(id+"F0.wireOp",EDGE,"E2.2"),sQuery(id+"F0.wireOp",EDGE,"E2.3")])],"isStart":false}),makeQuery(id+"F17.opExtrude","CAP_FACE",FACE,{"disambiguationData":[OSD([sQuery(id+"F16.wireOp",EDGE,"E93"),sQuery(id+"F16.wireOp",EDGE,"E94"),sQuery(id+"F16.wireOp",EDGE,"E98"),sQuery(id+"F16.wireOp",EDGE,"E102")])],"isStart":true}),makeQuery(id+"F17.opExtrude","CAP_FACE",FACE,{"disambiguationData":[OSD([sQuery(id+"F16.wireOp",EDGE,"E95.bottom"),sQuery(id+"F16.wireOp",EDGE,"E95.left"),sQuery(id+"F16.wireOp",EDGE,"E95.right"),sQuery(id+"F16.wireOp",EDGE,"E99")])],"isStart":true}),makeQuery(id+"F17.opExtrude","CAP_FACE",FACE,{"disambiguationData":[OSD([sQuery(id+"F16.wireOp",EDGE,"E96.bottom"),sQuery(id+"F16.wireOp",EDGE,"E96.left"),sQuery(id+"F16.wireOp",EDGE,"E96.right"),sQuery(id+"F16.wireOp",EDGE,"E101")])],"isStart":true}),makeQuery(id+"F17.opExtrude","CAP_FACE",FACE,{"disambiguationData":[OSD([sQuery(id+"F16.wireOp",EDGE,"E97.bottom"),sQuery(id+"F16.wireOp",EDGE,"E97.left"),sQuery(id+"F16.wireOp",EDGE,"E97.right"),sQuery(id+"F16.wireOp",EDGE,"E100")])],"isStart":true})]});
            var sketch = newSketch(context, id + "F18", { "sketchPlane" : qUnion([Q0])});
            skLineSegment(sketch, "E103", {"start": v(-30.76, 67.75) * mm, "end": v(27.37, 67.75) * mm});
            skLineSegment(sketch, "E104", {"start": v(27.37, 67.75) * mm, "end": v(27.37, 69.75) * mm});
            skLineSegment(sketch, "E105", {"start": v(37.37, 69.75) * mm, "end": v(37.37, -73.15) * mm});
            skLineSegment(sketch, "E106", {"start": v(27.37, -71.15) * mm, "end": v(27.37, -73.15) * mm});
            skArc(sketch, "E107", {"start": v(27.37, -73.15) * mm, "mid": v(32.37, -78.15) * mm, "end": v(37.37, -73.15) * mm});
            skArc(sketch, "E108", {"start": v(-40.76, -73.15) * mm, "mid": v(-35.76, -78.15) * mm, "end": v(-30.76, -73.15) * mm});
            skArc(sketch, "E109", {"start": v(37.37, 69.75) * mm, "mid": v(32.37, 74.75) * mm, "end": v(27.37, 69.75) * mm});
            skArc(sketch, "E110", {"start": v(-30.76, 69.75) * mm, "mid": v(-35.76, 74.75) * mm, "end": v(-40.76, 69.75) * mm});
            skLineSegment(sketch, "E111", {"start": v(-30.76, 67.75) * mm, "end": v(-30.76, 69.75) * mm});
            skLineSegment(sketch, "E112", {"start": v(-40.76, 69.75) * mm, "end": v(-40.76, -73.15) * mm});
            skLineSegment(sketch, "E113", {"start": v(-30.76, -73.15) * mm, "end": v(-30.76, -71.15) * mm});
            skLineSegment(sketch, "E114", {"start": v(-30.76, -71.15) * mm, "end": v(27.37, -71.15) * mm});
            skSolve(sketch);
        }
        {
            var Q0;
            Q0 = qSketchRegion(id + "F18", true);
            extrude(context, id + "F19", {"entities" : qUnion([Q0]), "depth" : 4 * mm, "offsetDistance" : 25 * mm});
        }
        {
            var Q0;
            Q0=makeQuery(id+"F19.opExtrude","CAP_FACE",FACE,{"disambiguationData":[OSD([sQuery(id+"F18.wireOp",EDGE,"E103"),sQuery(id+"F18.wireOp",EDGE,"E104"),sQuery(id+"F18.wireOp",EDGE,"E105"),sQuery(id+"F18.wireOp",EDGE,"E106"),sQuery(id+"F18.wireOp",EDGE,"E107"),sQuery(id+"F18.wireOp",EDGE,"E108"),sQuery(id+"F18.wireOp",EDGE,"E109"),sQuery(id+"F18.wireOp",EDGE,"E110"),sQuery(id+"F18.wireOp",EDGE,"E111"),sQuery(id+"F18.wireOp",EDGE,"E112"),sQuery(id+"F18.wireOp",EDGE,"E113"),sQuery(id+"F18.wireOp",EDGE,"E114")])],"isStart":true});
            var sketch = newSketch(context, id + "F20", { "sketchPlane" : qUnion([Q0])});
            skLineSegment(sketch, "E115.0", {"start": v(-37.96, -64.95) * mm, "end": v(34.57, -64.95) * mm});
            skLineSegment(sketch, "E115.1", {"start": v(-37.96, 68.35) * mm, "end": v(-37.96, -64.95) * mm});
            skLineSegment(sketch, "E115.2", {"start": v(-37.96, 68.35) * mm, "end": v(34.57, 68.35) * mm});
            skLineSegment(sketch, "E115.3", {"start": v(34.57, 68.35) * mm, "end": v(34.57, -64.95) * mm});
            skSolve(sketch);
        }
        {
            var Q0;
            Q0 = qSketchRegion(id + "F20", true);
            extrude(context, id + "F21", {"entities" : qUnion([Q0]), "operationType" : NewBodyOperationType.ADD, "depth" : 2 * mm, "offsetDistance" : 25 * mm});
        }
        {
            var Q0;
            Q0=makeQuery(id+"F19.opExtrude","CAP_FACE",FACE,{"disambiguationData":[OSD([sQuery(id+"F18.wireOp",EDGE,"E103"),sQuery(id+"F18.wireOp",EDGE,"E104"),sQuery(id+"F18.wireOp",EDGE,"E105"),sQuery(id+"F18.wireOp",EDGE,"E106"),sQuery(id+"F18.wireOp",EDGE,"E107"),sQuery(id+"F18.wireOp",EDGE,"E108"),sQuery(id+"F18.wireOp",EDGE,"E109"),sQuery(id+"F18.wireOp",EDGE,"E110"),sQuery(id+"F18.wireOp",EDGE,"E111"),sQuery(id+"F18.wireOp",EDGE,"E112"),sQuery(id+"F18.wireOp",EDGE,"E113"),sQuery(id+"F18.wireOp",EDGE,"E114")])],"isStart":false});
            var sketch = newSketch(context, id + "F22", { "sketchPlane" : qUnion([Q0])});
            skLineSegment(sketch, "E116", {"start": v(-1.7, -58.15) * mm, "end": v(21.8, -58.15) * mm});
            skLineSegment(sketch, "E117", {"start": v(21.8, -55.15) * mm, "end": v(-25.2, -55.15) * mm});
            skLineSegment(sketch, "E118", {"start": v(-25.2, -58.15) * mm, "end": v(-1.7, -58.15) * mm});
            skArc(sketch, "E119", {"start": v(-25.2, -55.15) * mm, "mid": v(-26.7, -56.65) * mm, "end": v(-25.2, -58.15) * mm});
            skArc(sketch, "E120", {"start": v(21.8, -58.15) * mm, "mid": v(23.3, -56.65) * mm, "end": v(21.8, -55.15) * mm});
            skPoint(sketch, "E121.start.orphan", {"position": v(23.3, -56.65) * mm});
            skLineSegment(sketch, "E122.0.1.0", {"start": v(21.8, -45.25) * mm, "end": v(-25.2, -45.25) * mm});
            skArc(sketch, "E122.0.1.1", {"start": v(-25.2, -45.25) * mm, "mid": v(-26.7, -46.75) * mm, "end": v(-25.2, -48.25) * mm});
            skLineSegment(sketch, "E122.0.1.2", {"start": v(-25.2, -48.25) * mm, "end": v(-1.7, -48.25) * mm});
            skLineSegment(sketch, "E122.0.1.3", {"start": v(-1.7, -48.25) * mm, "end": v(21.8, -48.25) * mm});
            skPoint(sketch, "E122.0.1.4", {"position": v(23.3, -46.75) * mm});
            skArc(sketch, "E122.0.1.5", {"start": v(21.8, -48.25) * mm, "mid": v(23.3, -46.75) * mm, "end": v(21.8, -45.25) * mm});
            skLineSegment(sketch, "E122.0.2.0", {"start": v(21.8, -35.35) * mm, "end": v(-25.2, -35.35) * mm});
            skArc(sketch, "E122.0.2.1", {"start": v(-25.2, -35.35) * mm, "mid": v(-26.7, -36.85) * mm, "end": v(-25.2, -38.35) * mm});
            skLineSegment(sketch, "E122.0.2.2", {"start": v(-25.2, -38.35) * mm, "end": v(-1.7, -38.35) * mm});
            skLineSegment(sketch, "E122.0.2.3", {"start": v(-1.7, -38.35) * mm, "end": v(21.8, -38.35) * mm});
            skPoint(sketch, "E122.0.2.4", {"position": v(23.3, -36.85) * mm});
            skArc(sketch, "E122.0.2.5", {"start": v(21.8, -38.35) * mm, "mid": v(23.3, -36.85) * mm, "end": v(21.8, -35.35) * mm});
            skLineSegment(sketch, "E122.0.3.0", {"start": v(21.8, -25.45) * mm, "end": v(-25.2, -25.45) * mm});
            skArc(sketch, "E122.0.3.1", {"start": v(-25.2, -25.45) * mm, "mid": v(-26.7, -26.95) * mm, "end": v(-25.2, -28.45) * mm});
            skLineSegment(sketch, "E122.0.3.2", {"start": v(-25.2, -28.45) * mm, "end": v(-1.7, -28.45) * mm});
            skLineSegment(sketch, "E122.0.3.3", {"start": v(-1.7, -28.45) * mm, "end": v(21.8, -28.45) * mm});
            skPoint(sketch, "E122.0.3.4", {"position": v(23.3, -26.95) * mm});
            skArc(sketch, "E122.0.3.5", {"start": v(21.8, -28.45) * mm, "mid": v(23.3, -26.95) * mm, "end": v(21.8, -25.45) * mm});
            skLineSegment(sketch, "E122.0.4.0", {"start": v(21.8, -15.55) * mm, "end": v(-25.2, -15.55) * mm});
            skArc(sketch, "E122.0.4.1", {"start": v(-25.2, -15.55) * mm, "mid": v(-26.7, -17.05) * mm, "end": v(-25.2, -18.55) * mm});
            skLineSegment(sketch, "E122.0.4.2", {"start": v(-25.2, -18.55) * mm, "end": v(-1.7, -18.55) * mm});
            skLineSegment(sketch, "E122.0.4.3", {"start": v(-1.7, -18.55) * mm, "end": v(21.8, -18.55) * mm});
            skPoint(sketch, "E122.0.4.4", {"position": v(23.3, -17.05) * mm});
            skArc(sketch, "E122.0.4.5", {"start": v(21.8, -18.55) * mm, "mid": v(23.3, -17.05) * mm, "end": v(21.8, -15.55) * mm});
            skLineSegment(sketch, "E122.0.5.0", {"start": v(21.8, -5.65) * mm, "end": v(-25.2, -5.65) * mm});
            skArc(sketch, "E122.0.5.1", {"start": v(-25.2, -5.65) * mm, "mid": v(-26.7, -7.15) * mm, "end": v(-25.2, -8.65) * mm});
            skLineSegment(sketch, "E122.0.5.2", {"start": v(-25.2, -8.65) * mm, "end": v(-1.7, -8.65) * mm});
            skLineSegment(sketch, "E122.0.5.3", {"start": v(-1.7, -8.65) * mm, "end": v(21.8, -8.65) * mm});
            skPoint(sketch, "E122.0.5.4", {"position": v(23.3, -7.15) * mm});
            skArc(sketch, "E122.0.5.5", {"start": v(21.8, -8.65) * mm, "mid": v(23.3, -7.15) * mm, "end": v(21.8, -5.65) * mm});
            skLineSegment(sketch, "E122.0.6.0", {"start": v(21.8, 4.25) * mm, "end": v(-25.2, 4.25) * mm});
            skArc(sketch, "E122.0.6.1", {"start": v(-25.2, 4.25) * mm, "mid": v(-26.7, 2.75) * mm, "end": v(-25.2, 1.25) * mm});
            skLineSegment(sketch, "E122.0.6.2", {"start": v(-25.2, 1.25) * mm, "end": v(-1.7, 1.25) * mm});
            skLineSegment(sketch, "E122.0.6.3", {"start": v(-1.7, 1.25) * mm, "end": v(21.8, 1.25) * mm});
            skPoint(sketch, "E122.0.6.4", {"position": v(23.3, 2.75) * mm});
            skArc(sketch, "E122.0.6.5", {"start": v(21.8, 1.25) * mm, "mid": v(23.3, 2.75) * mm, "end": v(21.8, 4.25) * mm});
            skLineSegment(sketch, "E122.0.7.0", {"start": v(21.8, 14.15) * mm, "end": v(-25.2, 14.15) * mm});
            skArc(sketch, "E122.0.7.1", {"start": v(-25.2, 14.15) * mm, "mid": v(-26.7, 12.65) * mm, "end": v(-25.2, 11.15) * mm});
            skLineSegment(sketch, "E122.0.7.2", {"start": v(-25.2, 11.15) * mm, "end": v(-1.7, 11.15) * mm});
            skLineSegment(sketch, "E122.0.7.3", {"start": v(-1.7, 11.15) * mm, "end": v(21.8, 11.15) * mm});
            skPoint(sketch, "E122.0.7.4", {"position": v(23.3, 12.65) * mm});
            skArc(sketch, "E122.0.7.5", {"start": v(21.8, 11.15) * mm, "mid": v(23.3, 12.65) * mm, "end": v(21.8, 14.15) * mm});
            skLineSegment(sketch, "E122.0.8.0", {"start": v(21.8, 24.05) * mm, "end": v(-25.2, 24.05) * mm});
            skArc(sketch, "E122.0.8.1", {"start": v(-25.2, 24.05) * mm, "mid": v(-26.7, 22.55) * mm, "end": v(-25.2, 21.05) * mm});
            skLineSegment(sketch, "E122.0.8.2", {"start": v(-25.2, 21.05) * mm, "end": v(-1.7, 21.05) * mm});
            skLineSegment(sketch, "E122.0.8.3", {"start": v(-1.7, 21.05) * mm, "end": v(21.8, 21.05) * mm});
            skPoint(sketch, "E122.0.8.4", {"position": v(23.3, 22.55) * mm});
            skArc(sketch, "E122.0.8.5", {"start": v(21.8, 21.05) * mm, "mid": v(23.3, 22.55) * mm, "end": v(21.8, 24.05) * mm});
            skLineSegment(sketch, "E122.0.9.0", {"start": v(21.8, 33.95) * mm, "end": v(-25.2, 33.95) * mm});
            skArc(sketch, "E122.0.9.1", {"start": v(-25.2, 33.95) * mm, "mid": v(-26.7, 32.45) * mm, "end": v(-25.2, 30.95) * mm});
            skLineSegment(sketch, "E122.0.9.2", {"start": v(-25.2, 30.95) * mm, "end": v(-1.7, 30.95) * mm});
            skLineSegment(sketch, "E122.0.9.3", {"start": v(-1.7, 30.95) * mm, "end": v(21.8, 30.95) * mm});
            skPoint(sketch, "E122.0.9.4", {"position": v(23.3, 32.45) * mm});
            skArc(sketch, "E122.0.9.5", {"start": v(21.8, 30.95) * mm, "mid": v(23.3, 32.45) * mm, "end": v(21.8, 33.95) * mm});
            skLineSegment(sketch, "E122.0.10.0", {"start": v(21.8, 43.85) * mm, "end": v(-25.2, 43.85) * mm});
            skArc(sketch, "E122.0.10.1", {"start": v(-25.2, 43.85) * mm, "mid": v(-26.7, 42.35) * mm, "end": v(-25.2, 40.85) * mm});
            skLineSegment(sketch, "E122.0.10.2", {"start": v(-25.2, 40.85) * mm, "end": v(-1.7, 40.85) * mm});
            skLineSegment(sketch, "E122.0.10.3", {"start": v(-1.7, 40.85) * mm, "end": v(21.8, 40.85) * mm});
            skPoint(sketch, "E122.0.10.4", {"position": v(23.3, 42.35) * mm});
            skArc(sketch, "E122.0.10.5", {"start": v(21.8, 40.85) * mm, "mid": v(23.3, 42.35) * mm, "end": v(21.8, 43.85) * mm});
            skLineSegment(sketch, "E122.0.11.0", {"start": v(21.8, 53.75) * mm, "end": v(-25.2, 53.75) * mm});
            skArc(sketch, "E122.0.11.1", {"start": v(-25.2, 53.75) * mm, "mid": v(-26.7, 52.25) * mm, "end": v(-25.2, 50.75) * mm});
            skLineSegment(sketch, "E122.0.11.2", {"start": v(-25.2, 50.75) * mm, "end": v(-1.7, 50.75) * mm});
            skLineSegment(sketch, "E122.0.11.3", {"start": v(-1.7, 50.75) * mm, "end": v(21.8, 50.75) * mm});
            skPoint(sketch, "E122.0.11.4", {"position": v(23.3, 52.25) * mm});
            skArc(sketch, "E122.0.11.5", {"start": v(21.8, 50.75) * mm, "mid": v(23.3, 52.25) * mm, "end": v(21.8, 53.75) * mm});
            skLineSegment(sketch, "E122.direction1", {"start": v(-25.2, -58.15) * mm, "end": v(-0.2, -58.15) * mm, "construction": true});
            skLineSegment(sketch, "E122.direction2", {"start": v(-25.2, -58.15) * mm, "end": v(-25.2, -48.25) * mm, "construction": true});
            skSolve(sketch);
        }
        {
            var Q0;
            Q0 = qSketchRegion(id + "F22", true);
            extrude(context, id + "F23", {"entities" : qUnion([Q0]), "operationType" : NewBodyOperationType.REMOVE, "oppositeDirection" : true, "depth" : 10 * mm, "offsetDistance" : 25 * mm});
        }
        {
            var Q0;
            Q0=makeQuery(id+"F19.opExtrude","CAP_FACE",FACE,{"disambiguationData":[OSD([sQuery(id+"F18.wireOp",EDGE,"E103"),sQuery(id+"F18.wireOp",EDGE,"E104"),sQuery(id+"F18.wireOp",EDGE,"E105"),sQuery(id+"F18.wireOp",EDGE,"E106"),sQuery(id+"F18.wireOp",EDGE,"E107"),sQuery(id+"F18.wireOp",EDGE,"E108"),sQuery(id+"F18.wireOp",EDGE,"E109"),sQuery(id+"F18.wireOp",EDGE,"E110"),sQuery(id+"F18.wireOp",EDGE,"E111"),sQuery(id+"F18.wireOp",EDGE,"E112"),sQuery(id+"F18.wireOp",EDGE,"E113"),sQuery(id+"F18.wireOp",EDGE,"E114")])],"isStart":false});
            var sketch = newSketch(context, id + "F24", { "sketchPlane" : qUnion([Q0])});
            skCircle(sketch, "E123", {"center": v(-35.76, 69.75) * mm, "radius": 1.3 * mm});
            skCircle(sketch, "E124", {"center": v(32.37, 69.75) * mm, "radius": 1.3 * mm});
            skCircle(sketch, "E125", {"center": v(-35.76, -73.15) * mm, "radius": 1.3 * mm});
            skCircle(sketch, "E126", {"center": v(32.37, -73.15) * mm, "radius": 1.3 * mm});
            skSolve(sketch);
        }
        {
            var Q0;
            Q0 = qSketchRegion(id + "F24", true);
            extrude(context, id + "F25", {"entities" : qUnion([Q0]), "operationType" : NewBodyOperationType.REMOVE, "oppositeDirection" : true, "depth" : 20 * mm, "offsetDistance" : 25 * mm});
        }
        {
            var Q0;
            Q0=makeQuery(id+"F17.boolean.opBoolean","MERGE",FACE,{"derivedFrom":[makeQuery(id+"F7.opExtrude","CAP_FACE",FACE,{"disambiguationData":[OSD([sQuery(id+"F0.wireOp",EDGE,"E1.0"),sQuery(id+"F0.wireOp",EDGE,"E1.1"),sQuery(id+"F0.wireOp",EDGE,"E1.2"),sQuery(id+"F0.wireOp",EDGE,"E1.3"),sQuery(id+"F0.wireOp",EDGE,"E2.0"),sQuery(id+"F0.wireOp",EDGE,"E2.1"),sQuery(id+"F0.wireOp",EDGE,"E2.2"),sQuery(id+"F0.wireOp",EDGE,"E2.3")])],"isStart":false}),makeQuery(id+"F17.opExtrude","CAP_FACE",FACE,{"disambiguationData":[OSD([sQuery(id+"F16.wireOp",EDGE,"E93"),sQuery(id+"F16.wireOp",EDGE,"E94"),sQuery(id+"F16.wireOp",EDGE,"E98"),sQuery(id+"F16.wireOp",EDGE,"E102")])],"isStart":true}),makeQuery(id+"F17.opExtrude","CAP_FACE",FACE,{"disambiguationData":[OSD([sQuery(id+"F16.wireOp",EDGE,"E95.bottom"),sQuery(id+"F16.wireOp",EDGE,"E95.left"),sQuery(id+"F16.wireOp",EDGE,"E95.right"),sQuery(id+"F16.wireOp",EDGE,"E99")])],"isStart":true}),makeQuery(id+"F17.opExtrude","CAP_FACE",FACE,{"disambiguationData":[OSD([sQuery(id+"F16.wireOp",EDGE,"E96.bottom"),sQuery(id+"F16.wireOp",EDGE,"E96.left"),sQuery(id+"F16.wireOp",EDGE,"E96.right"),sQuery(id+"F16.wireOp",EDGE,"E101")])],"isStart":true}),makeQuery(id+"F17.opExtrude","CAP_FACE",FACE,{"disambiguationData":[OSD([sQuery(id+"F16.wireOp",EDGE,"E97.bottom"),sQuery(id+"F16.wireOp",EDGE,"E97.left"),sQuery(id+"F16.wireOp",EDGE,"E97.right"),sQuery(id+"F16.wireOp",EDGE,"E100")])],"isStart":true})]});
            var sketch = newSketch(context, id + "F26", { "sketchPlane" : qUnion([Q0])});
            skCircle(sketch, "E127", {"center": v(-35.76, 69.75) * mm, "radius": 1.3 * mm});
            skCircle(sketch, "E128", {"center": v(32.37, 69.75) * mm, "radius": 1.3 * mm});
            skCircle(sketch, "E129", {"center": v(32.37, -73.15) * mm, "radius": 1.3 * mm});
            skCircle(sketch, "E130", {"center": v(-35.76, -73.15) * mm, "radius": 1.3 * mm});
            skSolve(sketch);
        }
        {
            var Q0;
            Q0 = qSketchRegion(id + "F26", true);
            extrude(context, id + "F27", {"entities" : qUnion([Q0]), "operationType" : NewBodyOperationType.REMOVE, "oppositeDirection" : true, "depth" : 15 * mm, "offsetDistance" : 25 * mm});
        }
        {
            var Q0;
            Q0=makeQuery(id+"F17.boolean.opBoolean","MERGE",FACE,{"derivedFrom":[makeQuery(id+"F3.boolean.opBoolean","MERGE",FACE,{"derivedFrom":[makeQuery(id+"F1.opExtrude","CAP_FACE",FACE,{"disambiguationData":[OSD([sQuery(id+"F0.wireOp",EDGE,"E1.0"),sQuery(id+"F0.wireOp",EDGE,"E1.1"),sQuery(id+"F0.wireOp",EDGE,"E1.2"),sQuery(id+"F0.wireOp",EDGE,"E1.3"),sQuery(id+"F0.wireOp",EDGE,"E2.0"),sQuery(id+"F0.wireOp",EDGE,"E2.1"),sQuery(id+"F0.wireOp",EDGE,"E2.2"),sQuery(id+"F0.wireOp",EDGE,"E2.3")])],"isStart":true}),makeQuery(id+"F3.opExtrude","CAP_FACE",FACE,{"disambiguationData":[OSD([sQuery(id+"F2.wireOp",EDGE,"E3.bottom"),sQuery(id+"F2.wireOp",EDGE,"E3.top"),sQuery(id+"F2.wireOp",EDGE,"E3.left"),sQuery(id+"F2.wireOp",EDGE,"E3.right")])],"isStart":true})]}),makeQuery(id+"F17.opExtrude","CAP_FACE",FACE,{"disambiguationData":[OSD([sQuery(id+"F16.wireOp",EDGE,"E93"),sQuery(id+"F16.wireOp",EDGE,"E94"),sQuery(id+"F16.wireOp",EDGE,"E98"),sQuery(id+"F16.wireOp",EDGE,"E102")])],"isStart":false}),makeQuery(id+"F17.opExtrude","CAP_FACE",FACE,{"disambiguationData":[OSD([sQuery(id+"F16.wireOp",EDGE,"E95.bottom"),sQuery(id+"F16.wireOp",EDGE,"E95.left"),sQuery(id+"F16.wireOp",EDGE,"E95.right"),sQuery(id+"F16.wireOp",EDGE,"E99")])],"isStart":false}),makeQuery(id+"F17.opExtrude","CAP_FACE",FACE,{"disambiguationData":[OSD([sQuery(id+"F16.wireOp",EDGE,"E96.bottom"),sQuery(id+"F16.wireOp",EDGE,"E96.left"),sQuery(id+"F16.wireOp",EDGE,"E96.right"),sQuery(id+"F16.wireOp",EDGE,"E101")])],"isStart":false}),makeQuery(id+"F17.opExtrude","CAP_FACE",FACE,{"disambiguationData":[OSD([sQuery(id+"F16.wireOp",EDGE,"E97.bottom"),sQuery(id+"F16.wireOp",EDGE,"E97.left"),sQuery(id+"F16.wireOp",EDGE,"E97.right"),sQuery(id+"F16.wireOp",EDGE,"E100")])],"isStart":false})]});
            var sketch = newSketch(context, id + "F28", { "sketchPlane" : qUnion([Q0])});
            skLineSegment(sketch, "E131", {"start": v(-35.76, 78.15) * mm, "end": v(32.37, 78.15) * mm});
            skLineSegment(sketch, "E132", {"start": v(32.37, 78.15) * mm, "end": v(32.37, 71.15) * mm});
            skLineSegment(sketch, "E133", {"start": v(32.37, 71.15) * mm, "end": v(-35.76, 71.15) * mm});
            skLineSegment(sketch, "E134", {"start": v(-35.76, 71.15) * mm, "end": v(-35.76, 78.15) * mm});
            skLineSegment(sketch, "E135", {"start": v(-35.76, -74.75) * mm, "end": v(32.37, -74.75) * mm});
            skLineSegment(sketch, "E136", {"start": v(32.37, -74.75) * mm, "end": v(32.37, -67.75) * mm});
            skLineSegment(sketch, "E137", {"start": v(32.37, -67.75) * mm, "end": v(-35.76, -67.75) * mm});
            skLineSegment(sketch, "E138", {"start": v(-35.76, -67.75) * mm, "end": v(-35.76, -74.75) * mm});
            skSolve(sketch);
        }
        {
            var Q0;
            Q0 = qSketchRegion(id + "F28", true);
            extrude(context, id + "F29", {"entities" : qUnion([Q0]), "operationType" : NewBodyOperationType.ADD, "oppositeDirection" : true, "depth" : 3.5 * mm, "offsetDistance" : 25 * mm});
        }
        {
            var Q0;
            Q0=makeQuery(id+"F29.opExtrude","CAP_FACE",FACE,{"disambiguationData":[OSD([sQuery(id+"F28.wireOp",EDGE,"E135"),sQuery(id+"F28.wireOp",EDGE,"E136"),sQuery(id+"F28.wireOp",EDGE,"E137"),sQuery(id+"F28.wireOp",EDGE,"E138")])],"isStart":false});
            var sketch = newSketch(context, id + "F30", { "sketchPlane" : qUnion([Q0])});
            skLineSegment(sketch, "E139", {"start": v(-30.76, 71.25) * mm, "end": v(-24.76, 71.25) * mm});
            skLineSegment(sketch, "E140", {"start": v(27.37, 71.25) * mm, "end": v(21.37, 71.25) * mm});
            skCircle(sketch, "E141", {"center": v(-24.76, 71.25) * mm, "radius": 1.25 * mm});
            skCircle(sketch, "E142", {"center": v(21.37, 71.25) * mm, "radius": 1.25 * mm});
            skSolve(sketch);
        }
        {
            var Q0;
            Q0 = qSketchRegion(id + "F30", true);
            extrude(context, id + "F31", {"entities" : qUnion([Q0]), "operationType" : NewBodyOperationType.REMOVE, "oppositeDirection" : true, "depth" : 25 * mm, "offsetDistance" : 25 * mm});
        }
        {
            var Q0;
            Q0=makeQuery(id+"F29.opExtrude","CAP_FACE",FACE,{"disambiguationData":[OSD([sQuery(id+"F28.wireOp",EDGE,"E131"),sQuery(id+"F28.wireOp",EDGE,"E132"),sQuery(id+"F28.wireOp",EDGE,"E133"),sQuery(id+"F28.wireOp",EDGE,"E134")])],"isStart":false});
            var sketch = newSketch(context, id + "F32", { "sketchPlane" : qUnion([Q0])});
            skLineSegment(sketch, "E143", {"start": v(-30.76, -74.65) * mm, "end": v(-24.76, -74.65) * mm});
            skLineSegment(sketch, "E144", {"start": v(27.37, -74.65) * mm, "end": v(21.37, -74.65) * mm});
            skCircle(sketch, "E145", {"center": v(21.37, -74.65) * mm, "radius": 1.25 * mm});
            skCircle(sketch, "E146", {"center": v(-24.76, -74.65) * mm, "radius": 1.25 * mm});
            skSolve(sketch);
        }
        {
            var Q0;
            Q0 = qSketchRegion(id + "F32", true);
            extrude(context, id + "F33", {"entities" : qUnion([Q0]), "operationType" : NewBodyOperationType.REMOVE, "oppositeDirection" : true, "depth" : 25 * mm, "offsetDistance" : 25 * mm});
        }
        {
            var Q0;
            {var subQ0=sQuery(id+"F0.wireOp",EDGE,"E2.0");Q0=makeQuery(id+"F7.boolean.opBoolean","MERGE",FACE,{"derivedFrom":[makeQuery(id+"F6.boolean.opBoolean","MERGE",FACE,{"derivedFrom":[makeQuery(id+"F1.opExtrude","SWEPT_FACE",FACE,{"disambiguationData":[OSD([subQ0])]}),makeQuery(id+"F6.opExtrude","SWEPT_FACE",FACE,{"disambiguationData":[OSD([subQ0])]})]}),makeQuery(id+"F7.opExtrude","SWEPT_FACE",FACE,{"disambiguationData":[OSD([subQ0])]})]});}
            var sketch = newSketch(context, id + "F34", { "sketchPlane" : qUnion([Q0])});
            skLineSegment(sketch, "E147", {"start": v(-30.76, 24.25) * mm, "end": v(-27.76, 24.25) * mm});
            skLineSegment(sketch, "E148", {"start": v(-27.76, 24.25) * mm, "end": v(-27.76, 38.25) * mm});
            skLineSegment(sketch, "E149", {"start": v(-25.76, 38.25) * mm, "end": v(-25.76, 10.25) * mm});
            skLineSegment(sketch, "E150", {"start": v(-27.76, 10.25) * mm, "end": v(-27.76, 24.25) * mm});
            skArc(sketch, "E151", {"start": v(-27.76, 10.25) * mm, "mid": v(-26.76, 9.25) * mm, "end": v(-25.76, 10.25) * mm});
            skArc(sketch, "E152", {"start": v(-25.76, 38.25) * mm, "mid": v(-26.76, 39.25) * mm, "end": v(-27.76, 38.25) * mm});
            skPoint(sketch, "E153.start.orphan", {"position": v(-26.76, 39.25) * mm});
            skPoint(sketch, "E154.start.orphan", {"position": v(-26.76, 9.25) * mm});
            skLineSegment(sketch, "E155.1.0.0", {"start": v(-18.6, 38.25) * mm, "end": v(-18.6, 10.25) * mm});
            skPoint(sketch, "E155.1.0.1", {"position": v(-19.6, 39.25) * mm});
            skPoint(sketch, "E155.1.0.2", {"position": v(-19.6, 9.25) * mm});
            skLineSegment(sketch, "E155.1.0.3", {"start": v(-20.6, 10.25) * mm, "end": v(-20.6, 24.25) * mm});
            skLineSegment(sketch, "E155.1.0.4", {"start": v(-20.6, 24.25) * mm, "end": v(-20.6, 38.25) * mm});
            skArc(sketch, "E155.1.0.5", {"start": v(-20.6, 10.25) * mm, "mid": v(-19.6, 9.25) * mm, "end": v(-18.6, 10.25) * mm});
            skArc(sketch, "E155.1.0.6", {"start": v(-18.6, 38.25) * mm, "mid": v(-19.6, 39.25) * mm, "end": v(-20.6, 38.25) * mm});
            skLineSegment(sketch, "E155.2.0.0", {"start": v(-11.44, 38.25) * mm, "end": v(-11.44, 10.25) * mm});
            skPoint(sketch, "E155.2.0.1", {"position": v(-12.44, 39.25) * mm});
            skPoint(sketch, "E155.2.0.2", {"position": v(-12.44, 9.25) * mm});
            skLineSegment(sketch, "E155.2.0.3", {"start": v(-13.44, 10.25) * mm, "end": v(-13.44, 24.25) * mm});
            skLineSegment(sketch, "E155.2.0.4", {"start": v(-13.44, 24.25) * mm, "end": v(-13.44, 38.25) * mm});
            skArc(sketch, "E155.2.0.5", {"start": v(-13.44, 10.25) * mm, "mid": v(-12.44, 9.25) * mm, "end": v(-11.44, 10.25) * mm});
            skArc(sketch, "E155.2.0.6", {"start": v(-11.44, 38.25) * mm, "mid": v(-12.44, 39.25) * mm, "end": v(-13.44, 38.25) * mm});
            skLineSegment(sketch, "E155.3.0.0", {"start": v(-4.28, 38.25) * mm, "end": v(-4.28, 10.25) * mm});
            skPoint(sketch, "E155.3.0.1", {"position": v(-5.28, 39.25) * mm});
            skPoint(sketch, "E155.3.0.2", {"position": v(-5.28, 9.25) * mm});
            skLineSegment(sketch, "E155.3.0.3", {"start": v(-6.28, 10.25) * mm, "end": v(-6.28, 24.25) * mm});
            skLineSegment(sketch, "E155.3.0.4", {"start": v(-6.28, 24.25) * mm, "end": v(-6.28, 38.25) * mm});
            skArc(sketch, "E155.3.0.5", {"start": v(-6.28, 10.25) * mm, "mid": v(-5.28, 9.25) * mm, "end": v(-4.28, 10.25) * mm});
            skArc(sketch, "E155.3.0.6", {"start": v(-4.28, 38.25) * mm, "mid": v(-5.28, 39.25) * mm, "end": v(-6.28, 38.25) * mm});
            skLineSegment(sketch, "E155.4.0.0", {"start": v(2.88, 38.25) * mm, "end": v(2.88, 10.25) * mm});
            skPoint(sketch, "E155.4.0.1", {"position": v(1.88, 39.25) * mm});
            skPoint(sketch, "E155.4.0.2", {"position": v(1.88, 9.25) * mm});
            skLineSegment(sketch, "E155.4.0.3", {"start": v(0.88, 10.25) * mm, "end": v(0.88, 24.25) * mm});
            skLineSegment(sketch, "E155.4.0.4", {"start": v(0.88, 24.25) * mm, "end": v(0.88, 38.25) * mm});
            skArc(sketch, "E155.4.0.5", {"start": v(0.88, 10.25) * mm, "mid": v(1.88, 9.25) * mm, "end": v(2.88, 10.25) * mm});
            skArc(sketch, "E155.4.0.6", {"start": v(2.88, 38.25) * mm, "mid": v(1.88, 39.25) * mm, "end": v(0.88, 38.25) * mm});
            skLineSegment(sketch, "E155.5.0.0", {"start": v(10.04, 38.25) * mm, "end": v(10.04, 10.25) * mm});
            skPoint(sketch, "E155.5.0.1", {"position": v(9.04, 39.25) * mm});
            skPoint(sketch, "E155.5.0.2", {"position": v(9.04, 9.25) * mm});
            skLineSegment(sketch, "E155.5.0.3", {"start": v(8.04, 10.25) * mm, "end": v(8.04, 24.25) * mm});
            skLineSegment(sketch, "E155.5.0.4", {"start": v(8.04, 24.25) * mm, "end": v(8.04, 38.25) * mm});
            skArc(sketch, "E155.5.0.5", {"start": v(8.04, 10.25) * mm, "mid": v(9.04, 9.25) * mm, "end": v(10.04, 10.25) * mm});
            skArc(sketch, "E155.5.0.6", {"start": v(10.04, 38.25) * mm, "mid": v(9.04, 39.25) * mm, "end": v(8.04, 38.25) * mm});
            skLineSegment(sketch, "E155.6.0.0", {"start": v(17.2, 38.25) * mm, "end": v(17.2, 10.25) * mm});
            skPoint(sketch, "E155.6.0.1", {"position": v(16.2, 39.25) * mm});
            skPoint(sketch, "E155.6.0.2", {"position": v(16.2, 9.25) * mm});
            skLineSegment(sketch, "E155.6.0.3", {"start": v(15.2, 10.25) * mm, "end": v(15.2, 24.25) * mm});
            skLineSegment(sketch, "E155.6.0.4", {"start": v(15.2, 24.25) * mm, "end": v(15.2, 38.25) * mm});
            skArc(sketch, "E155.6.0.5", {"start": v(15.2, 10.25) * mm, "mid": v(16.2, 9.25) * mm, "end": v(17.2, 10.25) * mm});
            skArc(sketch, "E155.6.0.6", {"start": v(17.2, 38.25) * mm, "mid": v(16.2, 39.25) * mm, "end": v(15.2, 38.25) * mm});
            skLineSegment(sketch, "E155.7.0.0", {"start": v(24.36, 38.25) * mm, "end": v(24.36, 10.25) * mm});
            skPoint(sketch, "E155.7.0.1", {"position": v(23.36, 39.25) * mm});
            skPoint(sketch, "E155.7.0.2", {"position": v(23.36, 9.25) * mm});
            skLineSegment(sketch, "E155.7.0.3", {"start": v(22.36, 10.25) * mm, "end": v(22.36, 24.25) * mm});
            skLineSegment(sketch, "E155.7.0.4", {"start": v(22.36, 24.25) * mm, "end": v(22.36, 38.25) * mm});
            skArc(sketch, "E155.7.0.5", {"start": v(22.36, 10.25) * mm, "mid": v(23.36, 9.25) * mm, "end": v(24.36, 10.25) * mm});
            skArc(sketch, "E155.7.0.6", {"start": v(24.36, 38.25) * mm, "mid": v(23.36, 39.25) * mm, "end": v(22.36, 38.25) * mm});
            skLineSegment(sketch, "E155.direction1", {"start": v(-26.76, 9.25) * mm, "end": v(-19.6, 9.25) * mm, "construction": true});
            skSolve(sketch);
        }
        {
            var Q0;
            Q0 = qSketchRegion(id + "F34", true);
            extrude(context, id + "F35", {"entities" : qUnion([Q0]), "operationType" : NewBodyOperationType.REMOVE, "oppositeDirection" : true, "depth" : 213 * mm, "offsetDistance" : 25 * mm});
        }
    });
